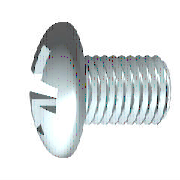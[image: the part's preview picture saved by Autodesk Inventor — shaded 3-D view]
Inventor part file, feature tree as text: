
AUTODESK INVENTOR PART (.ipt)
format: ipt  version: 2019 (Build 230136000, 136)  size: 274,944 bytes
history: native  units: mm (DEFAULTED — no unit token found)
features: extrude x1, other x1, plane x1
ambient origin geometry x7: Origin, YZ Plane, XZ Plane, X Axis, Y Axis, Z Axis, Center Point
bodies: Solid1 (feature_tree), Body (feature_tree)
feature tree (3):
  extrude  "Slot"  Depth=4.0mm
  other  "Cut"
  plane  "Work Plane3"
